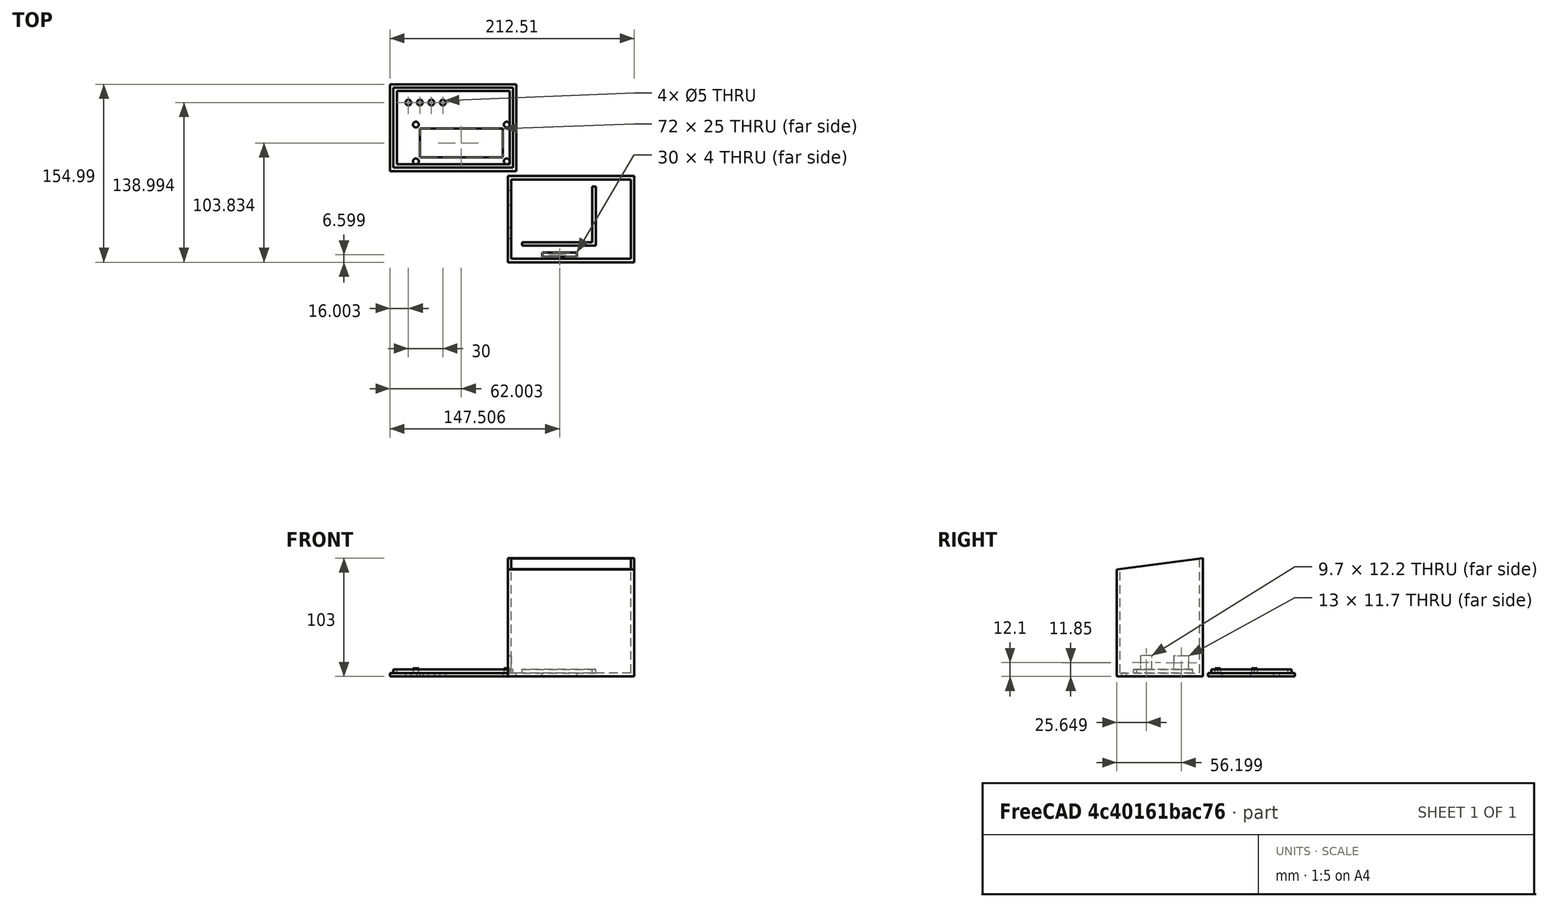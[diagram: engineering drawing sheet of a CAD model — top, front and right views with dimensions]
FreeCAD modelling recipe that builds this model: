
FCSTD DOCUMENT  (FreeCAD 0.19R)
Label: cube_timer_box
License: All rights reserved
LicenseURL: http://en.wikipedia.org/wiki/All_rights_reserved
objects: Sketcher::SketchObject×12, PartDesign::Pad×6, PartDesign::Pocket×6, PartDesign::Body×2
note: 38 computed .brp shape members not serialized (recipe doc carries the construction recipe); baked Part::Feature solids carry a one-line shape summary decoded from their .brp

FEATURE [Sketcher::SketchObject] Sketch
  FullyConstrained = false
  MapMode = 5
  Support = -> [XY_Plane]
  sketch-geometry (4):
    g0: LineSegment StartX=-45.3137 StartY=38.8491 StartZ=0 EndX=64.6863 EndY=38.8491 EndZ=0
    g1: LineSegment StartX=64.6863 StartY=38.8491 StartZ=0 EndX=64.6863 EndY=-36.1509 EndZ=0
    g2: LineSegment StartX=64.6863 StartY=-36.1509 StartZ=0 EndX=-45.3137 EndY=-36.1509 EndZ=0
    g3: LineSegment StartX=-45.3137 StartY=-36.1509 StartZ=0 EndX=-45.3137 EndY=38.8491 EndZ=0
  constraints (10):
    c: Coincident(g0,g1)
    c: Coincident(g1,g2)
    c: Coincident(g2,g3)
    c: Coincident(g3,g0)
    c: Horizontal(g0)
    c: Horizontal(g2)
    c: Vertical(g1)
    c: Vertical(g3)
    c: Distance(g1) = 75
    c: Distance(g0) = 110
FEATURE [PartDesign::Pad] Pad
  Direction = (1,1,1)
  Length = 3
  Length2 = 100
  Profile = -> Sketch
  Type = 0
FEATURE [Sketcher::SketchObject] Sketch001
  ExternalGeometry = -> [Pad]
  FullyConstrained = true
  MapMode = 5
  Placement = pos=(0,0,3) rot=(0,0,1;0rad)
  Support = -> [Pad]
  sketch-geometry (8):
    g0: LineSegment StartX=-45.3137 StartY=38.8491 StartZ=0 EndX=64.6863 EndY=38.8491 EndZ=0
    g1: LineSegment StartX=64.6863 StartY=38.8491 StartZ=0 EndX=64.6863 EndY=-36.1509 EndZ=0
    g2: LineSegment StartX=64.6863 StartY=-36.1509 StartZ=0 EndX=-45.3137 EndY=-36.1509 EndZ=0
    g3: LineSegment StartX=-45.3137 StartY=-36.1509 StartZ=0 EndX=-45.3137 EndY=38.8491 EndZ=0
    g4: LineSegment StartX=-42.3137 StartY=35.8491 StartZ=0 EndX=61.6863 EndY=35.8491 EndZ=0
    g5: LineSegment StartX=61.6863 StartY=35.8491 StartZ=0 EndX=61.6863 EndY=-33.1509 EndZ=0
    g6: LineSegment StartX=61.6863 StartY=-33.1509 StartZ=0 EndX=-42.3137 EndY=-33.1509 EndZ=0
    g7: LineSegment StartX=-42.3137 StartY=-33.1509 StartZ=0 EndX=-42.3137 EndY=35.8491 EndZ=0
  constraints (21):
    c: Coincident(g0,g1)
    c: Coincident(g1,g2)
    c: Coincident(g2,g3)
    c: Coincident(g3,g0)
    c: Horizontal(g2)
    c: Vertical(g3)
    c: Coincident(g4,g5)
    c: Coincident(g5,g6)
    c: Coincident(g6,g7)
    c: Coincident(g7,g4)
    c: Horizontal(g4)
    c: Horizontal(g6)
    c: Vertical(g5)
    c: Vertical(g7)
    c: DistanceX(g4,g0) = 3
    c: DistanceX(g0,g4) = 3
    c: DistanceY(g4,g0) = 3
    c: DistanceY(g1,g5) = 3
    c: Coincident(g0,g-6)
    c: Coincident(g0,g-4)
    c: Coincident(g1,g-5)
FEATURE [PartDesign::Pad] Pad001
  BaseFeature = -> Pad
  Direction = (1,1,1)
  Length = 100
  Length2 = 100
  Profile = -> Sketch001
  Type = 0
FEATURE [Sketcher::SketchObject] Sketch002
  ExternalGeometry = -> [Pad001]
  FullyConstrained = true
  MapMode = 5
  Placement = pos=(-45.3137,0,0) rot=(0.57735,-0.57735,-0.57735;2.0944rad)
  Support = -> [Pad001]
  sketch-geometry (3):
    g0: LineSegment StartX=-38.8491 StartY=103 StartZ=0 EndX=36.1509 EndY=93 EndZ=0
    g1: LineSegment StartX=36.1509 StartY=93 StartZ=0 EndX=36.1509 EndY=103 EndZ=0
    g2: LineSegment StartX=36.1509 StartY=103 StartZ=0 EndX=-38.8491 EndY=103 EndZ=0
  constraints (7):
    c: Coincident(g0,g1)
    c: Vertical(g1)
    c: Coincident(g1,g2)
    c: Coincident(g2,g0)
    c: Distance(g1) = 10
    c: Coincident(g0,g-3)
    c: Coincident(g1,g-4)
FEATURE [PartDesign::Pocket] Pocket
  BaseFeature = -> Pad001
  Length = 120
  Length2 = 100
  Profile = -> Sketch002
  Type = 0
FEATURE [Sketcher::SketchObject] Sketch003
  ExternalGeometry = -> [Pocket]
  FullyConstrained = true
  MapMode = 5
  Placement = pos=(-45.3137,0,0) rot=(0.57735,-0.57735,-0.57735;2.0944rad)
  Support = -> [Pocket]
  sketch-geometry (4):
    g0: LineSegment StartX=-26.5491 StartY=17.7 StartZ=0 EndX=-13.5491 EndY=17.7 EndZ=0
    g1: LineSegment StartX=-13.5491 StartY=17.7 StartZ=0 EndX=-13.5491 EndY=6 EndZ=0
    g2: LineSegment StartX=-13.5491 StartY=6 StartZ=0 EndX=-26.5491 EndY=6 EndZ=0
    g3: LineSegment StartX=-26.5491 StartY=6 StartZ=0 EndX=-26.5491 EndY=17.7 EndZ=0
  constraints (12):
    c: Coincident(g0,g1)
    c: Coincident(g1,g2)
    c: Coincident(g2,g3)
    c: Coincident(g3,g0)
    c: Horizontal(g0)
    c: Horizontal(g2)
    c: Vertical(g1)
    c: Vertical(g3)
    c: DistanceX(g-4,g2) = 12.3
    c: DistanceY(g-4,g2) = 3
    c: Distance(g1) = 11.7
    c: Distance(g0) = 13
FEATURE [PartDesign::Pocket] Pocket001
  BaseFeature = -> Pocket
  Length = 5
  Length2 = 100
  Profile = -> Sketch003
  Type = 0
FEATURE [Sketcher::SketchObject] Sketch004
  ExternalGeometry = -> [Pocket001]
  FullyConstrained = true
  MapMode = 5
  Placement = pos=(-45.3137,0,0) rot=(0.57735,-0.57735,-0.57735;2.0944rad)
  Support = -> [Pocket001]
  sketch-geometry (4):
    g0: LineSegment StartX=15.3509 StartY=6 StartZ=0 EndX=5.65091 EndY=6 EndZ=0
    g1: LineSegment StartX=5.65091 StartY=6 StartZ=0 EndX=5.65091 EndY=18.2 EndZ=0
    g2: LineSegment StartX=5.65091 StartY=18.2 StartZ=0 EndX=15.3509 EndY=18.2 EndZ=0
    g3: LineSegment StartX=15.3509 StartY=18.2 StartZ=0 EndX=15.3509 EndY=6 EndZ=0
  constraints (12):
    c: Coincident(g0,g1)
    c: Coincident(g1,g2)
    c: Coincident(g2,g3)
    c: Coincident(g3,g0)
    c: Horizontal(g0)
    c: Horizontal(g2)
    c: Vertical(g1)
    c: Vertical(g3)
    c: Distance(g2) = 9.7
    c: Distance(g1) = 12.2
    c: DistanceX(g-4,g0) = 19.2
    c: DistanceY(g-4,g0) = 0
FEATURE [PartDesign::Pocket] Pocket002
  BaseFeature = -> Pocket001
  Length = 5
  Length2 = 100
  Profile = -> Sketch004
  Type = 0
FEATURE [Sketcher::SketchObject] Sketch005
  ExternalGeometry = -> [Pocket002]
  FullyConstrained = true
  MapMode = 5
  Placement = pos=(0,0,0) rot=(1,0,0;3.14159rad)
  Support = -> [Pocket002]
  sketch-geometry (4):
    g0: LineSegment StartX=-15.3137 StartY=31.5509 StartZ=0 EndX=14.6863 EndY=31.5509 EndZ=0
    g1: LineSegment StartX=14.6863 StartY=31.5509 StartZ=0 EndX=14.6863 EndY=27.5509 EndZ=0
    g2: LineSegment StartX=14.6863 StartY=27.5509 StartZ=0 EndX=-15.3137 EndY=27.5509 EndZ=0
    g3: LineSegment StartX=-15.3137 StartY=27.5509 StartZ=0 EndX=-15.3137 EndY=31.5509 EndZ=0
  constraints (12):
    c: Coincident(g0,g1)
    c: Coincident(g1,g2)
    c: Coincident(g2,g3)
    c: Coincident(g3,g0)
    c: Horizontal(g0)
    c: Horizontal(g2)
    c: Vertical(g1)
    c: Vertical(g3)
    c: Distance(g0) = 30
    c: Distance(g1) = 4
    c: DistanceY(g0,g-3) = 4.6
    c: DistanceX(g-3,g0) = 30
FEATURE [PartDesign::Pocket] Pocket003
  BaseFeature = -> Pocket002
  Length = 5
  Length2 = 100
  Profile = -> Sketch005
  Type = 0
FEATURE [Sketcher::SketchObject] Sketch006
  ExternalGeometry = -> [Pocket003]
  FullyConstrained = false
  MapMode = 5
  Placement = pos=(0,0,3) rot=(0,0,1;0rad)
  Support = -> [Pocket003]
  sketch-geometry (6):
    g0: LineSegment StartX=-32.9334 StartY=-21.6509 StartZ=0 EndX=31.1863 EndY=-21.6509 EndZ=0
    g1: LineSegment StartX=31.1863 StartY=-21.6509 StartZ=0 EndX=31.1863 EndY=29.7967 EndZ=0
    g2: LineSegment StartX=31.1863 StartY=29.7967 StartZ=0 EndX=28.1863 EndY=29.7967 EndZ=0
    g3: LineSegment StartX=28.1863 StartY=29.7967 StartZ=0 EndX=28.1863 EndY=-18.6509 EndZ=0
    g4: LineSegment StartX=28.1863 StartY=-18.6509 StartZ=0 EndX=-32.9334 EndY=-18.6509 EndZ=0
    g5: LineSegment StartX=-32.9334 StartY=-18.6509 StartZ=0 EndX=-32.9334 EndY=-21.6509 EndZ=0
  constraints (16):
    c: Horizontal(g0)
    c: Coincident(g0,g1)
    c: Vertical(g1)
    c: Coincident(g1,g2)
    c: Horizontal(g2)
    c: Coincident(g2,g3)
    c: Vertical(g3)
    c: Coincident(g3,g4)
    c: Horizontal(g4)
    c: Coincident(g4,g5)
    c: Coincident(g5,g0)
    c: Perpendicular(g5,g4)
    c: DistanceX(g-3,g3) = 73.5
    c: DistanceY(g3,g-3) = 57.5
    c: Distance(g5) = 3
    c: Distance(g2) = 3
FEATURE [PartDesign::Pad] Pad002
  BaseFeature = -> Pocket003
  Direction = (1,1,1)
  Length = 3
  Length2 = 100
  Profile = -> Sketch006
  Type = 0
FEATURE [PartDesign::Body] Body  label="Box"
  Group = -> [Sketch,Pad,Sketch001,Pad001,Sketch002,Pocket,Sketch003,Pocket001,Sketch004,Pocket002,Sketch005,Pocket003,Sketch006,Pad002]
  Origin = -> Origin
  Tip = -> Pad002
FEATURE [Sketcher::SketchObject] Sketch007
  FullyConstrained = false
  MapMode = 5
  Support = -> [XY_Plane001]
  sketch-geometry (4):
    g0: LineSegment StartX=-147.817 StartY=118.844 StartZ=0 EndX=-37.8174 EndY=118.844 EndZ=0
    g1: LineSegment StartX=-37.8174 StartY=118.844 StartZ=0 EndX=-37.8174 EndY=43.1844 EndZ=0
    g2: LineSegment StartX=-37.8174 StartY=43.1844 StartZ=0 EndX=-147.817 EndY=43.1844 EndZ=0
    g3: LineSegment StartX=-147.817 StartY=43.1844 StartZ=0 EndX=-147.817 EndY=118.844 EndZ=0
  constraints (10):
    c: Coincident(g0,g1)
    c: Coincident(g1,g2)
    c: Coincident(g2,g3)
    c: Coincident(g3,g0)
    c: Horizontal(g0)
    c: Horizontal(g2)
    c: Vertical(g1)
    c: Vertical(g3)
    c: Distance(g0) = 110
    c: Distance(g1) = 75.66
FEATURE [PartDesign::Pad] Pad003
  Direction = (1,1,1)
  Length = 3
  Length2 = 100
  Profile = -> Sketch007
  Type = 0
FEATURE [Sketcher::SketchObject] Sketch009
  ExternalGeometry = -> [Pad003]
  FullyConstrained = true
  MapMode = 5
  Placement = pos=(0,0,3) rot=(0,0,1;0rad)
  Support = -> [Pad003]
  sketch-geometry (8):
    g0: LineSegment StartX=-144.817 StartY=115.844 StartZ=0 EndX=-40.8174 EndY=115.844 EndZ=0
    g1: LineSegment StartX=-40.8174 StartY=115.844 StartZ=0 EndX=-40.8174 EndY=46.1844 EndZ=0
    g2: LineSegment StartX=-40.8174 StartY=46.1844 StartZ=0 EndX=-144.817 EndY=46.1844 EndZ=0
    g3: LineSegment StartX=-144.817 StartY=46.1844 StartZ=0 EndX=-144.817 EndY=115.844 EndZ=0
    g4: LineSegment StartX=-141.817 StartY=112.844 StartZ=0 EndX=-43.8174 EndY=112.844 EndZ=0
    g5: LineSegment StartX=-43.8174 StartY=112.844 StartZ=0 EndX=-43.8174 EndY=49.1844 EndZ=0
    g6: LineSegment StartX=-43.8174 StartY=49.1844 StartZ=0 EndX=-141.817 EndY=49.1844 EndZ=0
    g7: LineSegment StartX=-141.817 StartY=49.1844 StartZ=0 EndX=-141.817 EndY=112.844 EndZ=0
  constraints (24):
    c: Coincident(g0,g1)
    c: Coincident(g1,g2)
    c: Coincident(g2,g3)
    c: Coincident(g3,g0)
    c: Horizontal(g0)
    c: Horizontal(g2)
    c: Vertical(g1)
    c: Vertical(g3)
    c: Coincident(g4,g5)
    c: Coincident(g5,g6)
    c: Coincident(g6,g7)
    c: Coincident(g7,g4)
    c: Horizontal(g4)
    c: Horizontal(g6)
    c: Vertical(g5)
    c: Vertical(g7)
    c: DistanceY(g0,g-4) = 3
    c: DistanceX(g-4,g0) = 3
    c: DistanceX(g0,g-3) = 3
    c: DistanceY(g-4,g2) = 3
    c: DistanceY(g4,g0) = 3
    c: DistanceX(g0,g4) = 3
    c: DistanceX(g4,g0) = 3
    c: DistanceY(g2,g6) = 3
FEATURE [PartDesign::Pad] Pad004
  BaseFeature = -> Pad003
  Direction = (1,1,1)
  Length = 3
  Length2 = 100
  Profile = -> Sketch009
  Type = 0
FEATURE [Sketcher::SketchObject] Sketch010
  ExternalGeometry = -> [Pad004]
  FullyConstrained = true
  MapMode = 5
  Placement = pos=(0,0,3) rot=(0,0,1;0rad)
  Support = -> [Pad004]
  sketch-geometry (4):
    g0: LineSegment StartX=-121.817 StartY=80.1844 StartZ=0 EndX=-49.8174 EndY=80.1844 EndZ=0
    g1: LineSegment StartX=-49.8174 StartY=80.1844 StartZ=0 EndX=-49.8174 EndY=55.1844 EndZ=0
    g2: LineSegment StartX=-49.8174 StartY=55.1844 StartZ=0 EndX=-121.817 EndY=55.1844 EndZ=0
    g3: LineSegment StartX=-121.817 StartY=55.1844 StartZ=0 EndX=-121.817 EndY=80.1844 EndZ=0
  constraints (12):
    c: Coincident(g0,g1)
    c: Coincident(g1,g2)
    c: Coincident(g2,g3)
    c: Coincident(g3,g0)
    c: Horizontal(g0)
    c: Horizontal(g2)
    c: Vertical(g1)
    c: Vertical(g3)
    c: Distance(g0) = 72
    c: Distance(g1) = 25
    c: DistanceX(g1,g-3) = 6
    c: DistanceY(g-3,g1) = 6
FEATURE [PartDesign::Pocket] Pocket004
  BaseFeature = -> Pad004
  Length = 5
  Length2 = 100
  Profile = -> Sketch010
  Type = 0
FEATURE [Sketcher::SketchObject] Sketch011
  ExternalGeometry = -> [Pocket004]
  FullyConstrained = true
  MapMode = 5
  Placement = pos=(0,0,3) rot=(0,0,1;0rad)
  Support = -> [Pocket004]
  sketch-geometry (4):
    g0: Circle CenterX=-131.817 CenterY=102.844 CenterZ=0 NormalX=0 NormalY=0 NormalZ=1 AngleXU=0 Radius=2.5
    g1: Circle CenterX=-121.817 CenterY=102.844 CenterZ=0 NormalX=0 NormalY=0 NormalZ=1 AngleXU=0 Radius=2.5
    g2: Circle CenterX=-111.817 CenterY=102.844 CenterZ=0 NormalX=0 NormalY=0 NormalZ=1 AngleXU=0 Radius=2.5
    g3: Circle CenterX=-101.817 CenterY=102.844 CenterZ=0 NormalX=0 NormalY=0 NormalZ=1 AngleXU=0 Radius=2.5
  constraints (12):
    c: Diameter(g0) = 5
    c: Diameter(g1) = 5
    c: Diameter(g2) = 5
    c: Diameter(g3) = 5
    c: DistanceX(g-3,g0) = 10
    c: DistanceY(g0,g-3) = 10
    c: DistanceY(g1,g0) = 0
    c: DistanceY(g2,g0) = 0
    c: DistanceY(g3,g0) = 0
    c: DistanceX(g0,g1) = 10
    c: DistanceX(g1,g2) = 10
    c: DistanceX(g2,g3) = 10
FEATURE [PartDesign::Pocket] Pocket005
  BaseFeature = -> Pocket004
  Length = 5
  Length2 = 100
  Profile = -> Sketch011
  Type = 0
FEATURE [Sketcher::SketchObject] Sketch012
  ExternalGeometry = -> [Pocket005]
  FullyConstrained = true
  MapMode = 5
  Placement = pos=(0,0,3) rot=(0,0,1;0rad)
  Support = -> [Pocket005]
  sketch-geometry (4):
    g0: Circle CenterX=-125.317 CenterY=83.6844 CenterZ=0 NormalX=0 NormalY=0 NormalZ=1 AngleXU=0 Radius=2.5
    g1: Circle CenterX=-46.3174 CenterY=83.6844 CenterZ=0 NormalX=0 NormalY=0 NormalZ=1 AngleXU=0 Radius=2.5
    g2: Circle CenterX=-46.3174 CenterY=51.6844 CenterZ=0 NormalX=0 NormalY=0 NormalZ=1 AngleXU=0 Radius=2.5
    g3: Circle CenterX=-125.317 CenterY=51.6844 CenterZ=0 NormalX=0 NormalY=0 NormalZ=1 AngleXU=0 Radius=2.5
  constraints (12):
    c: DistanceX(g0,g-3) = 3.5
    c: DistanceY(g-3,g0) = 3.5
    c: DistanceY(g-3,g1) = 3.5
    c: DistanceY(g2,g-4) = 3.5
    c: DistanceY(g3,g-4) = 3.5
    c: DistanceX(g3,g-4) = 3.5
    c: DistanceX(g-3,g1) = 3.5
    c: DistanceX(g-4,g2) = 3.5
    c: Diameter(g0) = 5
    c: Diameter(g1) = 5
    c: Diameter(g2) = 5
    c: Diameter(g3) = 5
FEATURE [PartDesign::Pad] Pad005
  BaseFeature = -> Pocket005
  Direction = (1,1,1)
  Length = 4
  Length2 = 100
  Profile = -> Sketch012
  Type = 0
FEATURE [PartDesign::Body] Body001  label="Lid"
  Group = -> [Sketch007,Pad003,Sketch009,Pad004,Sketch010,Pocket004,Sketch011,Pocket005,Sketch012,Pad005]
  Origin = -> Origin001
  Tip = -> Pad005
